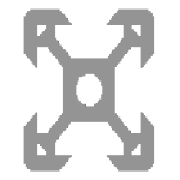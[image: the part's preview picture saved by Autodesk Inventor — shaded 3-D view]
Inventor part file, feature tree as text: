
AUTODESK INVENTOR PART (.ipt)
format: ipt  version: 2019 (Build 230136000, 136)  size: 198,656 bytes
history: native  units: mm
features: other x3, sketch x3, plane x1
ambient origin geometry x8: Origin, YZ Plane, XZ Plane, XY Plane, X Axis, Y Axis, Z Axis, Center Point
bodies: Solid1 (feature_tree), Body (feature_tree)
feature tree (7):
  other  "Driven Length"
  other  "Start Plane"
  other  "End Plane"
  sketch  "Sketch1"  dims[d2=4.2mm]
  sketch  "Sketch4"  dims[d3=1.5mm]
  plane  "Work Plane4"
  sketch  "Sketch5"  dims[d4=1.64mm d5=1.8mm d6=5.68mm d7=1.8mm d9=1.5mm d12=-0.0mm d13=550.0mm d14=0.13mm d15=0.0mm d18=90.0deg d17=550.0mm]
